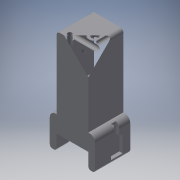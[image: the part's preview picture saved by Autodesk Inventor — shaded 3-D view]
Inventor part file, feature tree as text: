
AUTODESK INVENTOR PART (.ipt)
format: ipt  version: 2016 (Build 200138000, 138)  size: 457,216 bytes
history: native  units: mm
features: extrude x19, sketch x19, fillet x5
ambient origin geometry x8: Origin, YZ Plane, XZ Plane, XY Plane, X Axis, Y Axis, Z Axis, Center Point
bodies: Solid1 (feature_tree)
feature tree (43):
  extrude  "Extrusion1"  Depth=53.0mm
  extrude  "Extrusion2"  Depth=2.0mm
  extrude  "Extrusion3"  Depth=2.0mm
  extrude  "Extrusion4"  Depth=18.0mm TaperAngle=0.0deg
  extrude  "Extrusion5"  Depth=5.0mm
  extrude  "Extrusion7"  Depth=7.5mm
  extrude  "Extrusion9"  Depth=13.0mm TaperAngle=0.0deg
  extrude  "Extrusion8"  Depth=3.5mm TaperAngle=0.0deg
  extrude  "Extrusion10"  Depth=7.3mm
  sketch  "Sketch11"  dims[d35=7.3mm d36=3.5mm d37=0.0mm]
  fillet  "Fillet1"  Radius=2.0mm
  fillet  "Fillet2"  Radius=1.0mm
  extrude  "Extrusion12"  Depth=18.0mm TaperAngle=0.0deg
  extrude  "Extrusion15"  Depth=9.0mm
  extrude  "Extrusion16"  Depth=9.0mm
  fillet  "Fillet5"  Radius=26.0mm
  extrude  "Extrusion17"  Depth=18.0mm TaperAngle=0.0deg
  extrude  "Extrusion18"  Depth=2.0mm
  extrude  "Extrusion19"  Depth=1.5mm
  extrude  "Extrusion20"  Depth=0.5mm
  extrude  "Extrusion21"  Depth=7.0mm
  extrude  "Extrusion22"  Depth=19.0mm TaperAngle=0.0deg
  fillet  "Fillet6"  Radius=9.0mm
  fillet  "Fillet7"  Radius=10.0mm
  extrude  "Extrusion23"  Depth=4.0mm TaperAngle=0.0deg
  sketch  "Sketch1"  dims[d0=19.0mm d1=53.0mm]
  sketch  "Sketch2"  dims[d2=1.0mm d3=0.0mm d4=2.0mm]
  sketch  "Sketch5"  dims[d5=1.0mm d6=2.0mm]
  sketch  "Sketch6"  dims[d7=1.0mm d8=18.0mm d9=0.0mm]
  sketch  "Sketch7"  dims[d28=5.0mm d29=7.1mm]
  sketch  "Sketch9"  dims[d30=4.5mm d31=7.5mm]
  sketch  "Sketch10"  dims[d32=7.5mm d33=13.0mm d34=0.0mm]
  sketch  "Sketch12"  dims[d38=3.5mm d39=0.0mm d40=7.3mm d46=2.0mm d47=1.0mm]
  sketch  "Sketch16"  dims[d48=18.0mm d49=0.0mm d50=46.0mm d51=0.0mm]
  sketch  "Sketch20"  dims[d52=12.0mm d54=9.0mm]
  sketch  "Sketch21"  dims[d55=8.0mm d57=9.0mm d59=26.0mm]
  sketch  "Sketch22"  dims[d61=1.3mm d62=18.0mm d63=0.0mm]
  sketch  "Sketch23"  dims[d67=8.0mm d68=0.0mm d72=2.0mm]
  sketch  "Sketch24"  dims[d77=2.0mm d78=1.5mm]
  sketch  "Sketch25"  dims[d79=1.5mm d80=0.5mm]
  sketch  "Sketch28"  dims[d84=3.0mm d85=7.0mm]
  sketch  "Sketch29"  dims[d86=4.0mm d87=19.0mm d88=0.0mm d106=9.0mm d107=10.0mm]
  sketch  "Sketch30"  dims[d108=4.0mm d109=0.0mm d110=4.0mm d111=0.0mm d112=3.5mm d113=9.0mm d114=10.0mm d121=2.0mm d122=0.0mm d126=3.0mm d127=1.5mm d128=1.5mm d129=5.0mm d130=0.0mm d132=2.0mm d133=3.0mm d137=10.0mm d141=2.0mm d142=0.0mm d143=5.0mm d144=0.0mm d150=2.0mm d151=2.0mm d152=5.5mm d153=1.3mm d154=2.5mm d155=4.0mm d156=3.65mm d157=3.65mm d158=2.5mm d159=3.0mm d160=2.851448mm d161=10.0mm d162=0.0mm d163=2.5mm d164=2.1mm d165=2.1mm d166=1.5mm d167=10.0mm d168=0.0mm d169=0.0mm d170=2.0mm d171=2.0mm d172=1.5mm d173=3.5mm d175=1.0mm d176=1.0mm d177=3.5mm d178=0.0mm d179=1.0mm d180=2.0mm d181=0.0mm d182=2.5mm d183=1.0mm d184=4.0mm d185=26.3mm d186=0.0mm d187=0.15mm d189=0.25mm d190=2.0mm]
